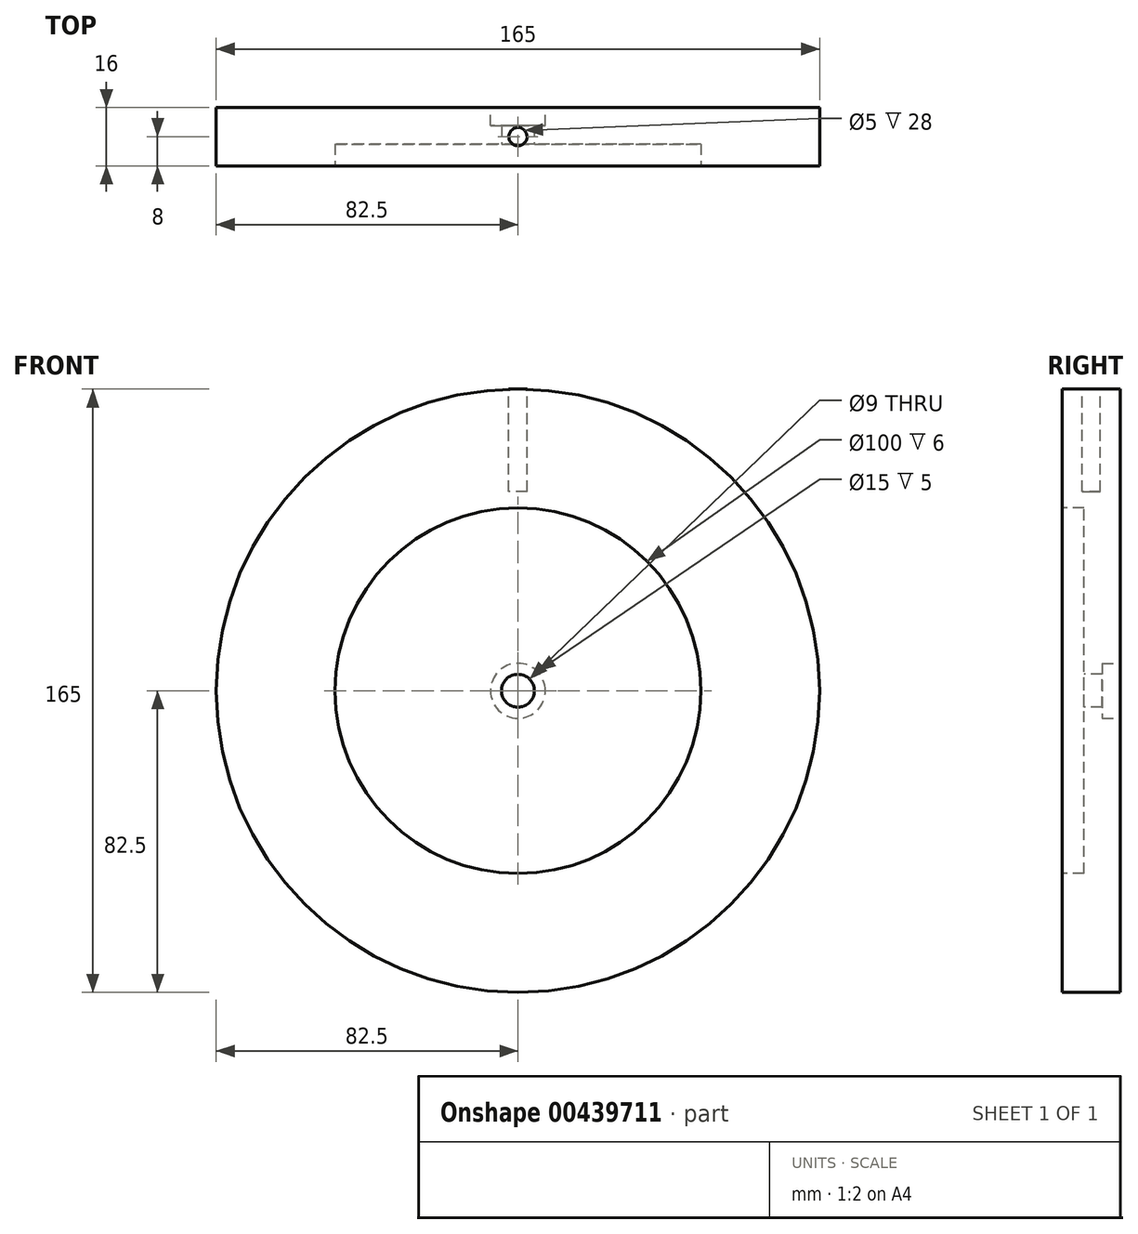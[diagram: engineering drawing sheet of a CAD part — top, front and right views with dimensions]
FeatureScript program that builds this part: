
annotation { "Feature Type Name" : "Feature", "Feature Type Description" : "" }
export const myFeature = defineFeature(function(context is Context, id is Id, definition is map)
    precondition{}
    {
        {
            var Q0;
            Q0=qCreatedBy(makeId("Front.planeOp"),FACE);
            var sketch = newSketch(context, id + "F0", { "sketchPlane" : qUnion([Q0])});
            skCircle(sketch, "E0", {"center": v(0, 0) * mm, "radius": 82.5 * mm});
            skSolve(sketch);
        }
        {
            var Q0;
            Q0=makeQuery(id+"F0.imprint","IMPRINT",FACE,{"disambiguationData":[TD([[makeQuery(id+"F0.imprint","IMPRINT",EDGE,{"derivedFrom":sQuery(id+"F0.wireOp",EDGE,"E0")}),1.0]])]});
            extrude(context, id + "F1", {"entities" : qUnion([Q0]), "depth" : 16 * mm});
        }
        {
            var Q0;
            Q0=makeQuery(id+"F1.opExtrude","CAP_FACE",FACE,{"disambiguationData":[OSD([sQuery(id+"F0.wireOp",EDGE,"E0")])],"isStart":false});
            var sketch = newSketch(context, id + "F2", { "sketchPlane" : qUnion([Q0])});
            skCircle(sketch, "E1", {"center": v(0, 0) * mm, "radius": 50 * mm});
            skSolve(sketch);
        }
        {
            var Q0;
            Q0=makeQuery(id+"F2.imprint","IMPRINT",FACE,{"disambiguationData":[TD([[makeQuery(id+"F2.imprint","IMPRINT",EDGE,{"derivedFrom":sQuery(id+"F2.wireOp",EDGE,"E1")}),1.0]])]});
            extrude(context, id + "F3", {"entities" : qUnion([Q0]), "operationType" : NewBodyOperationType.REMOVE, "oppositeDirection" : true, "depth" : 6 * mm});
        }
        {
            var Q0;
            Q0=qCreatedBy(makeId("Top.planeOp"),FACE);
            cPlane(context, id + "F4", {"entities" : qUnion([Q0]), "cplaneType" : CPlaneType.OFFSET, "offset" : (165 / 2) * mm, "width" : 150 * mm, "height" : 150 * mm});
        }
        {
            var Q0;
            Q0=qCreatedBy(id+"F4.planeOp",FACE);
            var sketch = newSketch(context, id + "F5", { "sketchPlane" : qUnion([Q0])});
            skLineSegment(sketch, "E2", {"start": v(0, 0) * mm, "end": v(0, -16) * mm});
            skCircle(sketch, "E3", {"center": v(0, -8) * mm, "radius": 2.5 * mm});
            skSolve(sketch);
        }
        {
            var Q0;
            {var subQ0=sQuery(id+"F5.wireOp",EDGE,"E3");var subQ1=sQuery(id+"F5.wireOp",EDGE,"E2");var subQ2=makeQuery(id+"F5.imprint","INTERSECT",VERTEX,{"disambiguationData":[OD(0.0)],"derivedFrom":[subQ1,subQ0]});Q0=makeQuery(id+"F5.imprint","IMPRINT",FACE,{"disambiguationData":[TD([[makeQuery(id+"F5.imprint","IMPRINT",EDGE,{"disambiguationData":[TD([[subQ2,1.0]])],"derivedFrom":subQ1}),1.0]])]});}
            var Q1;
            {var subQ0=sQuery(id+"F5.wireOp",EDGE,"E3");var subQ1=sQuery(id+"F5.wireOp",EDGE,"E2");var subQ2=makeQuery(id+"F5.imprint","INTERSECT",VERTEX,{"disambiguationData":[OD(0.0)],"derivedFrom":[subQ1,subQ0]});Q1=makeQuery(id+"F5.imprint","IMPRINT",FACE,{"disambiguationData":[TD([[makeQuery(id+"F5.imprint","IMPRINT",EDGE,{"disambiguationData":[TD([[subQ2,1.0]])],"derivedFrom":subQ1}),-1.0]])]});}
            extrude(context, id + "F6", {"entities" : qUnion([Q0, Q1]), "operationType" : NewBodyOperationType.REMOVE, "oppositeDirection" : true, "depth" : 28 * mm});
        }
        {
            var Q0;
            Q0=makeQuery(id+"F3.boolean.opBoolean","COPY",FACE,{"derivedFrom":makeQuery(id+"F3.opExtrude","CAP_FACE",FACE,{"disambiguationData":[OSD([sQuery(id+"F2.wireOp",EDGE,"E1")])],"isStart":false})});
            var sketch = newSketch(context, id + "F7", { "sketchPlane" : qUnion([Q0])});
            skCircle(sketch, "E4", {"center": v(0, 0) * mm, "radius": 4.5 * mm});
            skSolve(sketch);
        }
        {
            var Q0;
            Q0=makeQuery(id+"F7.imprint","IMPRINT",FACE,{"disambiguationData":[TD([[makeQuery(id+"F7.imprint","IMPRINT",EDGE,{"derivedFrom":sQuery(id+"F7.wireOp",EDGE,"E4")}),1.0]])]});
            extrude(context, id + "F8", {"entities" : qUnion([Q0]), "operationType" : NewBodyOperationType.REMOVE, "oppositeDirection" : true, "depth" : 25 * mm});
        }
        {
            var Q0;
            Q0=makeQuery(id+"F1.opExtrude","CAP_FACE",FACE,{"disambiguationData":[OSD([sQuery(id+"F0.wireOp",EDGE,"E0")])],"isStart":true});
            var sketch = newSketch(context, id + "F9", { "sketchPlane" : qUnion([Q0])});
            skCircle(sketch, "E5", {"center": v(0, 0) * mm, "radius": 7.5 * mm});
            skSolve(sketch);
        }
        {
            var Q0;
            Q0=makeQuery(id+"F9.imprint","IMPRINT",FACE,{"disambiguationData":[TD([[makeQuery(id+"F9.imprint","IMPRINT",EDGE,{"derivedFrom":sQuery(id+"F9.wireOp",EDGE,"E5")}),1.0]])]});
            extrude(context, id + "F10", {"entities" : qUnion([Q0]), "operationType" : NewBodyOperationType.REMOVE, "oppositeDirection" : true, "depth" : 5 * mm});
        }
    });
